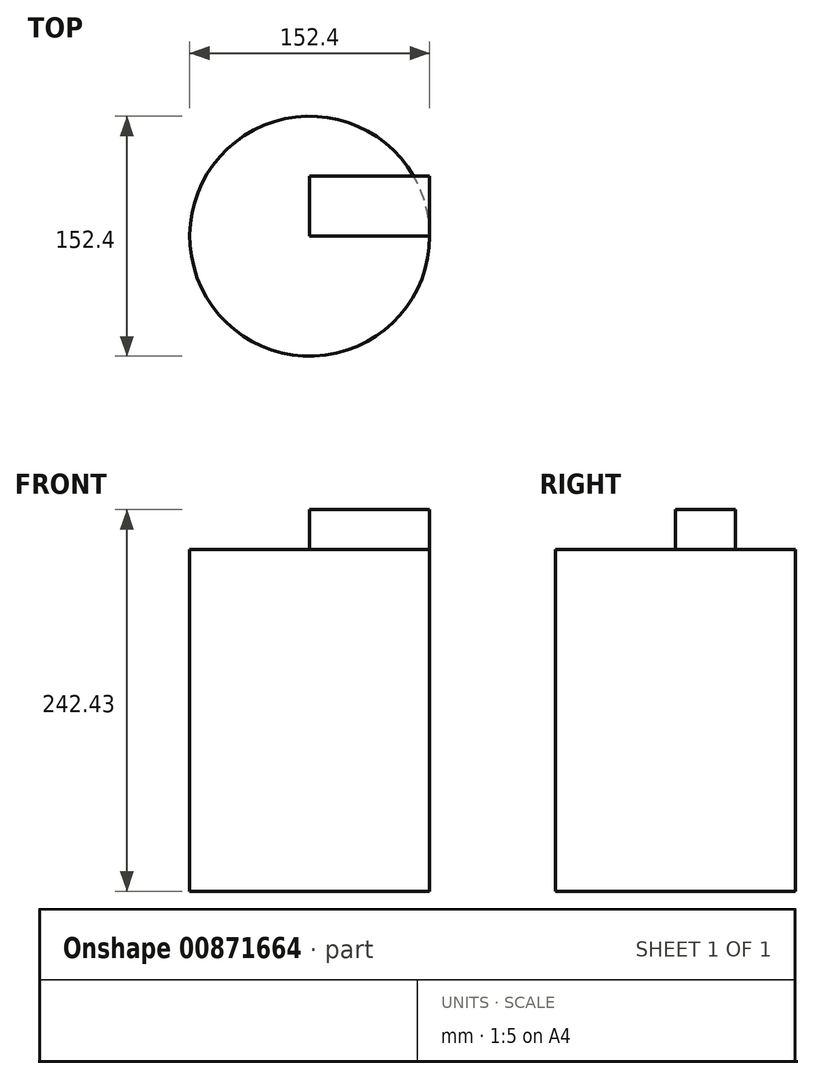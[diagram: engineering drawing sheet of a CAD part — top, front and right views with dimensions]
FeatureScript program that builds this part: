
annotation { "Feature Type Name" : "Feature", "Feature Type Description" : "" }
export const myFeature = defineFeature(function(context is Context, id is Id, definition is map)
    precondition{}
    {
        {
            var Q0;
            Q0=qCreatedBy(makeId("Top.planeOp"),FACE);
            var sketch = newSketch(context, id + "F0", { "sketchPlane" : qUnion([Q0])});
            skCircle(sketch, "E0", {"center": v(0, 0) * mm, "radius": 76.2 * mm});
            skSolve(sketch);
        }
        {
            var Q0;
            Q0=qCreatedBy(makeId("Top.planeOp"),FACE);
            var sketch = newSketch(context, id + "F1", { "sketchPlane" : qUnion([Q0])});
            skLineSegment(sketch, "E1.bottom", {"start": v(0, 0) * mm, "end": v(76.2, 0) * mm});
            skLineSegment(sketch, "E1.top", {"start": v(0, 38.1) * mm, "end": v(76.2, 38.1) * mm});
            skLineSegment(sketch, "E1.left", {"start": v(0, 0) * mm, "end": v(0, 38.1) * mm});
            skLineSegment(sketch, "E1.right", {"start": v(76.2, 0) * mm, "end": v(76.2, 38.1) * mm});
            skArc(sketch, "E2", {"start": v(19.05, 38.1) * mm, "mid": v(0, 19.05) * mm, "end": v(19.05, 0) * mm});
            skArc(sketch, "E3", {"start": v(57.15, 0) * mm, "mid": v(76.2, 19.05) * mm, "end": v(57.15, 38.1) * mm});
            skSolve(sketch);
        }
        {
            var Q0;
            Q0 = qSketchRegion(id + "F1", true);
            extrude(context, id + "F2", {"entities" : qUnion([Q0]), "depth" : 25.4 * mm, "offsetDistance" : 25.4 * mm});
        }
        {
            var Q0;
            Q0=makeQuery(id+"F0.imprint","IMPRINT",FACE,{"disambiguationData":[TD([[makeQuery(id+"F0.imprint","IMPRINT",EDGE,{"derivedFrom":sQuery(id+"F0.wireOp",EDGE,"E0")}),1.0]])]});
            var Q1;
            Q1=sQuery(id+"F0.wireOp",EDGE,"E0");
            extrude(context, id + "F3", {"entities" : qUnion([Q0]), "operationType" : NewBodyOperationType.ADD, "surfaceEntities" : qUnion([Q1]), "endBound" : BoundingType.THROUGH_ALL, "oppositeDirection" : true, "depth" : 152.4 * mm, "offsetDistance" : 25.4 * mm});
        }
        {
            var Q0;
            Q0=makeQuery(id+"F0.imprint","IMPRINT",FACE,{"disambiguationData":[TD([[makeQuery(id+"F0.imprint","IMPRINT",EDGE,{"derivedFrom":sQuery(id+"F0.wireOp",EDGE,"E0")}),1.0]])]});
            extrude(context, id + "F4", {"entities" : qUnion([Q0]), "operationType" : NewBodyOperationType.ADD, "oppositeDirection" : true, "depth" : 152.4 * mm, "offsetDistance" : 25.4 * mm});
        }
    });
